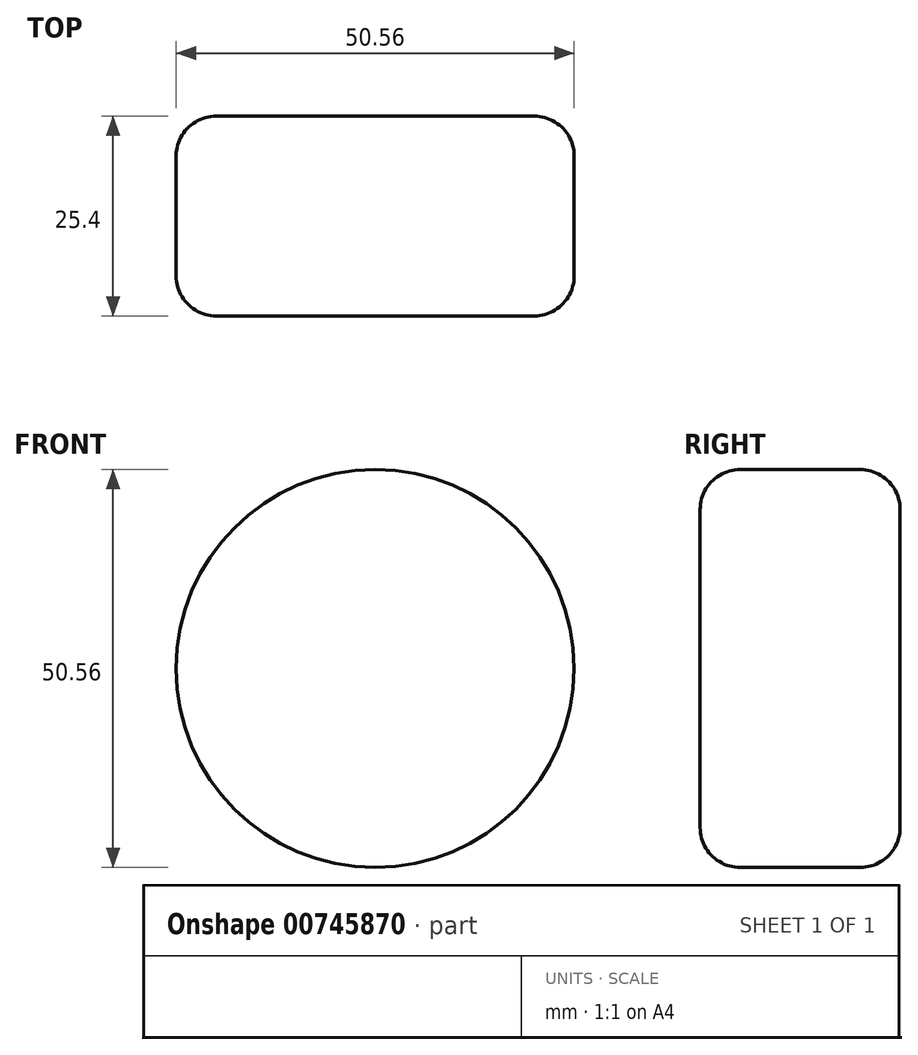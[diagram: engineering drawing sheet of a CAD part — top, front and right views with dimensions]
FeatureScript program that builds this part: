
annotation { "Feature Type Name" : "Feature", "Feature Type Description" : "" }
export const myFeature = defineFeature(function(context is Context, id is Id, definition is map)
    precondition{}
    {
        {
            var Q0;
            Q0=qCreatedBy(makeId("Front.planeOp"),FACE);
            var sketch = newSketch(context, id + "F0", { "sketchPlane" : qUnion([Q0])});
            skCircle(sketch, "E0", {"center": v(0, 0) * mm, "radius": 25.28 * mm});
            skSolve(sketch);
        }
        {
            var Q0;
            Q0 = qSketchRegion(id + "F0", true);
            extrude(context, id + "F1", {"entities" : qUnion([Q0]), "depth" : 25.4 * mm, "offsetDistance" : 25.4 * mm});
        }
        {
            var Q0;
            Q0=makeQuery(id+"F1.opExtrude","CAP_FACE",FACE,{"disambiguationData":[OSD([sQuery(id+"F0.wireOp",EDGE,"E0")])],"isStart":false});
            var Q1;
            Q1=makeQuery(id+"F1.opExtrude","CAP_FACE",FACE,{"disambiguationData":[OSD([sQuery(id+"F0.wireOp",EDGE,"E0")])],"isStart":true});
            fillet(context, id + "F2", {"entities" : qUnion([Q0, Q1]), "radius" : 5.08 * mm, "tangentPropagation" : true, "allowEdgeOverflow" : false});
        }
    });
